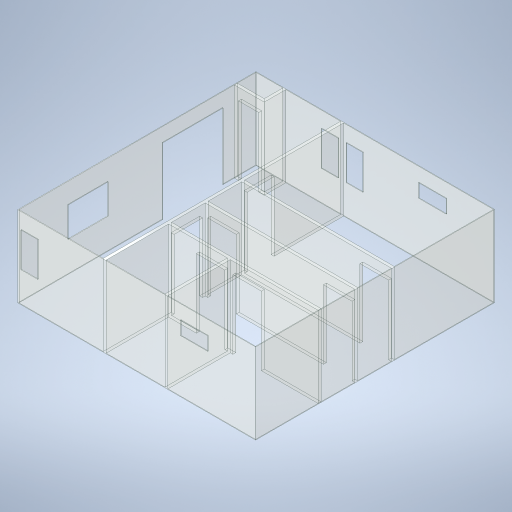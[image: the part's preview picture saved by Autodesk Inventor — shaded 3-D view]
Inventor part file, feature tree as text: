
AUTODESK INVENTOR PART (.ipt)
format: ipt  version: 2024.1 (Build 281209000, 209)  size: 536,576 bytes
history: native  units: in
note: dims shown in document units (in); Inventor stores cm internally (conversion verified against a paired STEP export)
features: extrude x17, sketch x17
ambient origin geometry x8: Origin, YZ Plane, XZ Plane, XY Plane, X Axis, Y Axis, Z Axis, Center Point
bodies: Solid1 (feature_tree)
feature tree (34):
  extrude  "Extrusion1"  Depth=0.5in
  extrude  "Extrusion2"  Depth=284.0in
  extrude  "Extrusion4"  Depth=96.0in TaperAngle=0.0deg
  extrude  "Extrusion5"  Depth=3.5in
  extrude  "Extrusion6"  Depth=70.0in
  extrude  "Extrusion7"  Depth=32.5in
  extrude  "Extrusion8"  Depth=96.0in TaperAngle=0.0deg
  extrude  "Extrusion9"  Depth=16.0in
  extrude  "Extrusion10"  Depth=57.0in
  extrude  "Extrusion11"  Depth=39.25in
  extrude  "Extrusion14"  Depth=72.0in
  extrude  "Extrusion15"  Depth=107.0in
  extrude  "Extrusion21"  Depth=47.5in
  extrude  "Extrusion22"  Depth=41.0in
  extrude  "Extrusion24"  Depth=3.0in
  extrude  "Extrusion25"  Depth=20.0in TaperAngle=0.0deg
  extrude  "Extrusion26"  Depth=36.0in
  sketch  "Sketch1"  dims[d1=284.0in d2=0.5in]
  sketch  "Sketch2"  dims[d4=283.0in d5=284.0in]
  sketch  "Sketch5"  dims[d6=0.75in d26=96.0in d27=0.0in]
  sketch  "Sketch6"  dims[d34=96.0in d35=0.0in d41=3.5in]
  sketch  "Sketch7"  dims[d44=104.25in d45=70.0in]
  sketch  "Sketch8"  dims[d51=79.0in d53=32.5in]
  sketch  "Sketch9"  dims[d54=16.0in d55=96.0in d56=0.0in]
  sketch  "Sketch10"  dims[d57=79.0in d58=16.0in]
  sketch  "Sketch11"  dims[d59=33.0in d60=57.0in]
  sketch  "Sketch12"  dims[d61=1.0in d62=0.0in d63=39.25in]
  sketch  "Sketch15"  dims[d64=79.0in d65=72.0in]
  sketch  "Sketch16"  dims[d66=1.0in d67=0.0in d71=107.0in]
  sketch  "Sketch22"  dims[d72=35.5in d73=47.5in]
  sketch  "Sketch23"  dims[d74=1.0in d75=0.0in d76=41.0in]
  sketch  "Sketch24"  dims[d77=36.0in d78=3.0in]
  sketch  "Sketch25"  dims[d79=20.0in d80=1.0in d81=0.0in]
  sketch  "Sketch26"  dims[d82=3.0in d83=36.0in d84=20.0in d85=41.0in d86=1.0in d87=0.0in d90=32.0in d91=6.5in d92=24.0in d93=96.0in d94=0.0in d95=82.0in d96=3.0in d97=34.0in d98=82.0in d99=1.0in d100=0.0in d111=36.0in d113=41.0in d114=20.0in d115=3.0in d116=36.0in d117=1.0in d118=0.0in d122=3.0in d123=34.0in d124=82.0in d125=1.0in d126=0.0in d137=40.0in d138=20.0in d139=20.0in d156=32.0in d157=82.0in d158=1.0in d159=0.0in d160=3.0in d161=82.0in d162=34.0in d163=1.0in d164=0.0in d166=57.0in d169=3.0in d170=34.0in d171=82.0in d172=1.0in d173=0.0in d174=3.0in d175=82.0in d176=34.0in d177=1.0in d178=0.0in d179=3.0in d180=82.0in d181=34.0in d182=1.0in d183=0.0in d184=3.0in d185=25.75in d36=0.5in d37=0.0344in d140=0.0344in]
